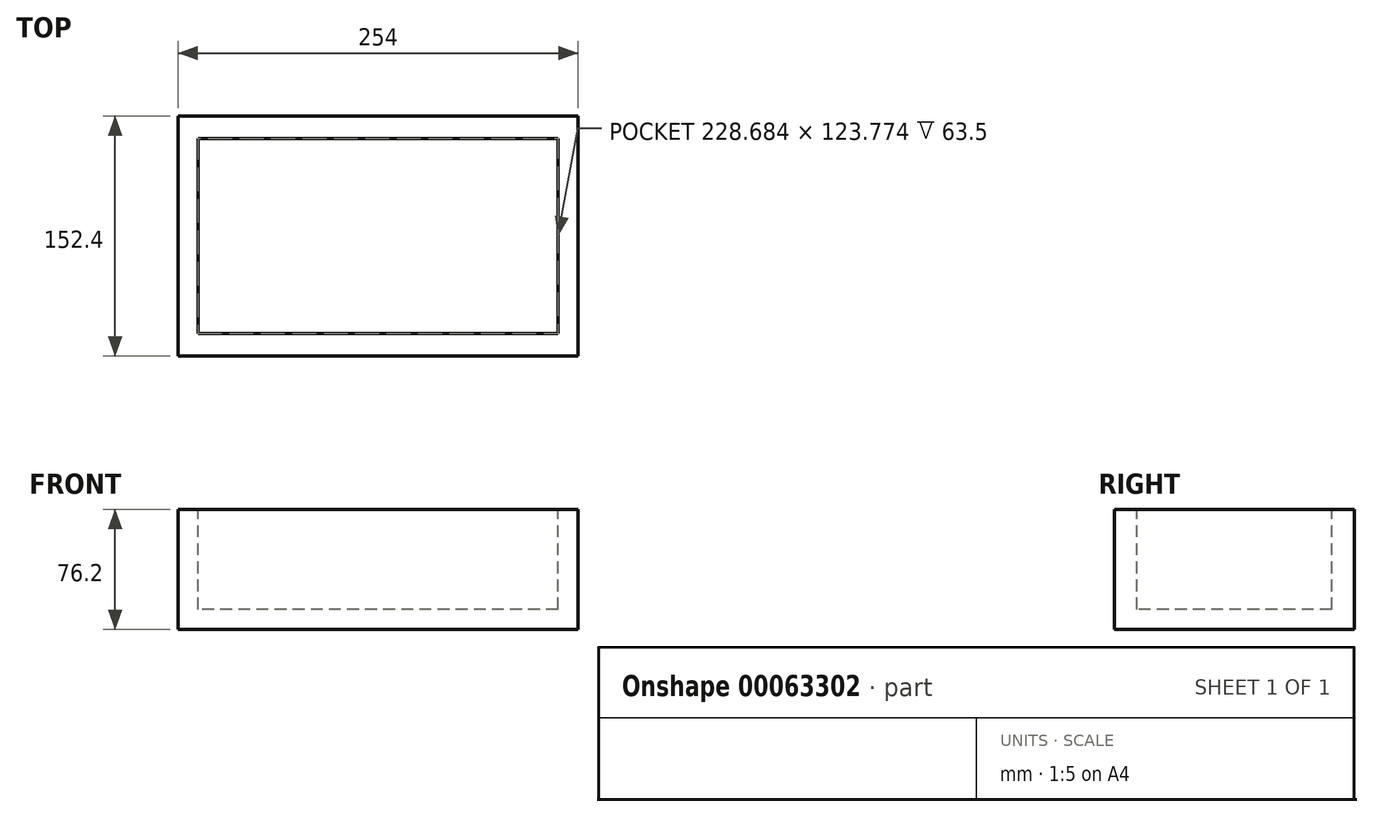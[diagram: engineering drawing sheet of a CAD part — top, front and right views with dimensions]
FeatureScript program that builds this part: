
annotation { "Feature Type Name" : "Feature", "Feature Type Description" : "" }
export const myFeature = defineFeature(function(context is Context, id is Id, definition is map)
    precondition{}
    {
        {
            var Q0;
            Q0=qCreatedBy(makeId("Top.planeOp"),FACE);
            var sketch = newSketch(context, id + "F0", { "sketchPlane" : qUnion([Q0])});
            skLineSegment(sketch, "E0.rect.bottom", {"start": v(127, 76.2) * mm, "end": v(-127, 76.2) * mm});
            skLineSegment(sketch, "E0.rect.top", {"start": v(127, -76.2) * mm, "end": v(-127, -76.2) * mm});
            skLineSegment(sketch, "E0.rect.left", {"start": v(127, 76.2) * mm, "end": v(127, -76.2) * mm});
            skLineSegment(sketch, "E0.rect.right", {"start": v(-127, 76.2) * mm, "end": v(-127, -76.2) * mm});
            skPoint(sketch, "E0.rect.middle", {"position": v(0, 0) * mm});
            skSolve(sketch);
        }
        {
            var Q0;
            Q0=makeQuery(id+"F0.imprint","IMPRINT",FACE,{"disambiguationData":[TD([[makeQuery(id+"F0.imprint","IMPRINT",EDGE,{"derivedFrom":sQuery(id+"F0.wireOp",EDGE,"E0.rect.bottom")}),1.0]])]});
            extrude(context, id + "F1", {"entities" : qUnion([Q0]), "depth" : 76.2 * mm, "symmetric" : true});
        }
        {
            var Q0;
            Q0=makeQuery(id+"F1.opExtrude","CAP_FACE",FACE,{"disambiguationData":[OSD([sQuery(id+"F0.wireOp",EDGE,"E0.rect.bottom"),sQuery(id+"F0.wireOp",EDGE,"E0.rect.top"),sQuery(id+"F0.wireOp",EDGE,"E0.rect.left"),sQuery(id+"F0.wireOp",EDGE,"E0.rect.right")])],"isStart":false});
            var sketch = newSketch(context, id + "F2", { "sketchPlane" : qUnion([Q0])});
            skLineSegment(sketch, "E1.rect.bottom", {"start": v(114.34, 61.89) * mm, "end": v(-114.34, 61.89) * mm});
            skLineSegment(sketch, "E1.rect.top", {"start": v(114.34, -61.89) * mm, "end": v(-114.34, -61.89) * mm});
            skLineSegment(sketch, "E1.rect.left", {"start": v(114.34, 61.89) * mm, "end": v(114.34, -61.89) * mm});
            skLineSegment(sketch, "E1.rect.right", {"start": v(-114.34, 61.89) * mm, "end": v(-114.34, -61.89) * mm});
            skPoint(sketch, "E1.rect.middle", {"position": v(0, 0) * mm});
            skSolve(sketch);
        }
        {
            var Q0;
            Q0=makeQuery(id+"F2.imprint","IMPRINT",FACE,{"disambiguationData":[TD([[makeQuery(id+"F2.imprint","IMPRINT",EDGE,{"derivedFrom":sQuery(id+"F2.wireOp",EDGE,"E1.rect.bottom")}),1.0]])]});
            var Q1;
            Q1 = qSketchRegion(id + "F2", true);
            extrude(context, id + "F3", {"entities" : qUnion([Q0, Q1]), "operationType" : NewBodyOperationType.REMOVE, "oppositeDirection" : true, "depth" : 63.5 * mm});
        }
    });
